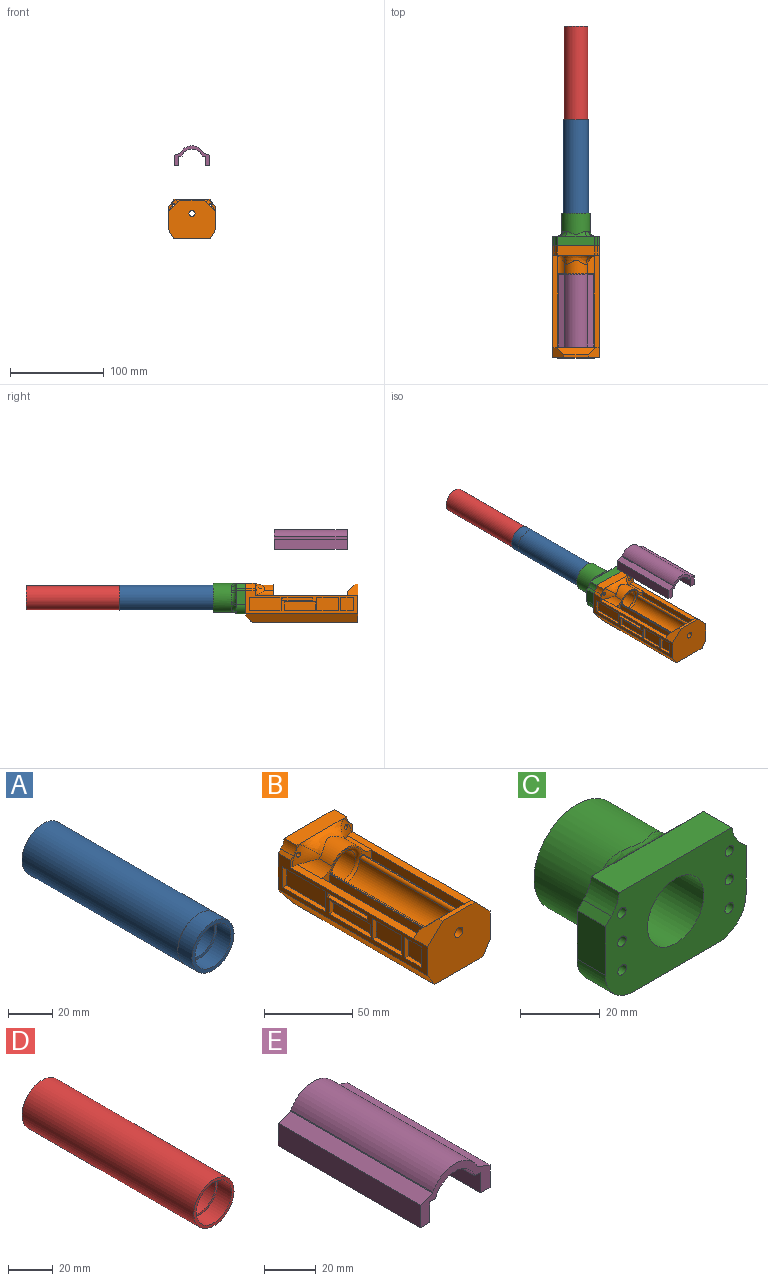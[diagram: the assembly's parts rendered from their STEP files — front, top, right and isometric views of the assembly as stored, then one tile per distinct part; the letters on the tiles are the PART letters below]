
ASSEMBLY  parts=5 mates=4
PART A: 12 faces, bbox 27.1x109x27.1 mm
  f0: plane 22.5x22.5mm, normal (0,1,0), area 83.4mm2, adj f2,f9
  f1: plane 23x23mm, normal (0,-1,0), area 101.3mm2, adj f2,f6
  f2: cylinder r=10mm len=100mm, axis (0,-1,0), area 6283.2mm2, adj f0,f1
  f3: cylinder r=13.55mm len=100mm, axis (0,-1,0), area 8513.7mm2, adj f4,f5
  f4: plane 27.1x27.1mm, normal (0,1,0), area 66.1mm2, adj f3,f10
  f5: plane 27.1x27.1mm, normal (0,-1,0), area 4.2mm2, adj f3,f7
  f6: cylinder r=11.5mm len=23mm, axis (0,1,0), area 650.3mm2, adj f1,f8
  f7: cylinder r=13.5mm len=27mm, axis (0,1,0), area 763.4mm2, adj f5,f8
  f8: plane 27x27mm, normal (0,-1,0), area 157.1mm2, adj f6,f7
  f9: cylinder r=11.25mm len=22.5mm, axis (0,1,0), area 706.9mm2, adj f0,f11
  f10: cylinder r=12.75mm len=25.5mm, axis (0,1,0), area 801.1mm2, adj f4,f11
  f11: plane 25.5x25.5mm, normal (0,1,0), area 113.1mm2, adj f9,f10
PART B: 129 faces, bbox 66.7x120x48.3 mm
  f0: plane 8.42x1.15mm, normal (0,0,-1), area 9.6mm2, adj f9,f13,f119,f127
  f1: plane 98.88x5.35mm, normal (0,0,1), area 514.2mm2, adj f5,f7,f103,f104,f105,f109,f119
  f2: plane 78.85x0.69mm, normal (0,0,1), area 54.5mm2, adj f103,f111,f119,f126
  f3: plane 78.85x0.69mm, normal (0,0,1), area 54.5mm2, adj f103,f113,f119,f125
  f4: plane 98.88x5.35mm, normal (0,0,1), area 514.2mm2, adj f6,f12,f103,f107,f108,f115,f119
  f5: plane 13x6.97mm, normal (0,-1,0), area 17.7mm2, adj f1,f7,f14,f16,f19,f105
  f6: plane 13x6.97mm, normal (0,-1,0), area 17.7mm2, adj f4,f12,f14,f17,f18,f107
  f7: plane 120x25mm, normal (-1,0,0), area 1029.4mm2, adj f1,f5,f10,f11,f16,f30,f51,f52
  f8: plane 113x38.65mm, normal (0,0,-1), area 2240.3mm2, adj f10,f30,f31,f32,f34,f36,f37,f39
  f9: cylinder r=11mm len=80.76mm, axis (0,1,0), area 2885.8mm2, adj f0,f13,f118,f119,f124,f125,f126
  f10: plane 50x40.97mm, normal (0,-1,0), area 1820.1mm2, adj f7,f8,f12,f30,f31,f120,f122,f123
  f11: plane 50x34.97mm, normal (0,1,0), area 1338.2mm2, adj f7,f12,f14,f15,f16,f17,f18,f19
  f12: plane 120x25mm, normal (1,0,0), area 1029.4mm2, adj f4,f6,f10,f11,f17,f31,f76,f77
  f13: plane 22x13.66mm, normal (0,1,0), area 217.4mm2, adj f0,f9,f118,f127
  f14: plane 40x10mm, normal (0,0,1), area 400mm2, adj f5,f6,f11,f18,f19,f106
  f15: cylinder r=10mm len=27mm, axis (0,-1,0), area 1696.5mm2, adj f11,f124
  f16: plane 10x2.15mm, normal (-0.71,0,0.71), area 30.3mm2, adj f5,f7,f11,f19
  f17: plane 10x2.15mm, normal (0.71,0,0.71), area 30.3mm2, adj f6,f11,f12,f18
  f18: cylinder r=10mm len=10mm, axis (0,1,0), area 66.3mm2, adj f6,f11,f14,f17
  f19: cylinder r=10mm len=10mm, axis (0,1,0), area 66.3mm2, adj f5,f11,f14,f16
  f20: cylinder r=1.5mm len=10.52mm, axis (0,1,0), area 97.8mm2, adj f11,f107
  f21: cylinder r=1.5mm len=25mm, axis (0,1,0), area 235.6mm2, adj f11,f22
  f22: plane 3x3mm, normal (0,1,0), area 7.1mm2, adj f21
  f23: cylinder r=1.5mm len=25mm, axis (0,1,0), area 235.6mm2, adj f11,f24
  f24: plane 3x3mm, normal (0,1,0), area 7.1mm2, adj f23
  f25: cylinder r=1.5mm len=10.52mm, axis (0,1,0), area 97.8mm2, adj f11,f105
  f26: cylinder r=1.5mm len=25mm, axis (0,1,0), area 235.6mm2, adj f11,f27
  f27: plane 3x3mm, normal (0,1,0), area 7.1mm2, adj f26
  f28: cylinder r=1.5mm len=25mm, axis (0,1,0), area 235.6mm2, adj f11,f29
  f29: plane 3x3mm, normal (0,1,0), area 7.1mm2, adj f28
  f30: plane 120x8.97mm, normal (-0.85,0,-0.53), area 1244.6mm2, adj f7,f8,f10,f11,f101
  f31: plane 120x8.97mm, normal (0.85,0,-0.53), area 1244.6mm2, adj f8,f10,f11,f12,f101
  f32: cylinder r=7.5mm len=15mm, axis (0,0,-1), area 471.2mm2, adj f8,f33
  f33: plane 15x15mm, normal (0,0,-1), area 176.7mm2, adj f32
  f34: cylinder r=7.5mm len=15mm, axis (0,0,-1), area 471.2mm2, adj f8,f35
  f35: plane 15x15mm, normal (0,0,-1), area 176.7mm2, adj f34
  f36: plane 30x5mm, normal (0,1,0), area 150mm2, adj f8,f37,f39,f40
  f37: plane 18.57x5mm, normal (1,0,0), area 88.8mm2, adj f8,f36,f38,f40,f101
  f38: plane 30x2.17mm, normal (0,-1,0), area 65.1mm2, adj f37,f39,f40,f101
  f39: plane 18.57x5mm, normal (-1,0,0), area 88.8mm2, adj f8,f36,f38,f40,f101
  f40: plane 30x18.57mm, normal (0,0,-1), area 557.1mm2, adj f36,f37,f38,f39
  f41: plane 30x5mm, normal (0,1,0), area 150mm2, adj f8,f42,f44,f45
  f42: plane 26.66x5mm, normal (1,0,0), area 133.3mm2, adj f8,f41,f43,f45
  f43: plane 30x5mm, normal (0,-1,0), area 150mm2, adj f8,f42,f44,f45
  f44: plane 26.66x5mm, normal (-1,0,0), area 133.3mm2, adj f8,f41,f43,f45
  f45: plane 30x26.66mm, normal (0,0,-1), area 799.7mm2, adj f41,f42,f43,f44
  f46: plane 16.72x5mm, normal (-1,0,0), area 83.6mm2, adj f8,f47,f49,f50
  f47: plane 30x5mm, normal (0,1,0), area 150mm2, adj f8,f46,f48,f50
  f48: plane 16.72x5mm, normal (1,0,0), area 83.6mm2, adj f8,f47,f49,f50
  f49: plane 30x5mm, normal (0,-1,0), area 150mm2, adj f8,f46,f48,f50
  f50: plane 30x16.72mm, normal (0,0,-1), area 501.7mm2, adj f46,f47,f48,f49
  f51: plane 13.47x3mm, normal (0,0,-1), area 40.4mm2, adj f7,f52,f54,f55
  f52: plane 14.37x3mm, normal (0,-1,0), area 43.1mm2, adj f7,f51,f53,f55
  f53: plane 13.47x3mm, normal (0,0,1), area 40.4mm2, adj f7,f52,f54,f55
  f54: plane 14.37x3mm, normal (0,1,0), area 43.1mm2, adj f7,f51,f53,f55
  f55: plane 14.37x13.47mm, normal (-1,0,0), area 193.6mm2, adj f51,f52,f53,f54
  f56: plane 23.27x3mm, normal (0,0,-1), area 69.8mm2, adj f7,f57,f59,f60
  f57: plane 14.21x3mm, normal (0,-1,0), area 42.6mm2, adj f7,f56,f58,f60
  f58: plane 23.27x3mm, normal (0,0,1), area 69.8mm2, adj f7,f57,f59,f60
  f59: plane 14.21x3mm, normal (0,1,0), area 42.6mm2, adj f7,f56,f58,f60
  f60: plane 23.27x14.21mm, normal (-1,0,0), area 330.8mm2, adj f56,f57,f58,f59
  f61: plane 31.97x3mm, normal (0,0,-1), area 95.9mm2, adj f7,f62,f64,f65
  f62: plane 3.08x3mm, normal (0,-1,0), area 9.2mm2, adj f7,f61,f63,f65
  f63: plane 31.97x3mm, normal (0,0,1), area 95.9mm2, adj f7,f62,f64,f65
  f64: plane 3.08x3mm, normal (0,1,0), area 9.2mm2, adj f7,f61,f63,f65
  f65: plane 31.97x3.08mm, normal (-1,0,0), area 98.5mm2, adj f61,f62,f63,f64
  f66: plane 33.34x3mm, normal (0,0,-1), area 100mm2, adj f7,f67,f69,f70
  f67: plane 9.6x3mm, normal (0,-1,0), area 28.8mm2, adj f7,f66,f68,f70
  f68: plane 33.34x3mm, normal (0,0,1), area 100mm2, adj f7,f67,f69,f70
  f69: plane 9.6x3mm, normal (0,1,0), area 28.8mm2, adj f7,f66,f68,f70
  f70: plane 33.34x9.6mm, normal (-1,0,0), area 320mm2, adj f66,f67,f68,f69
  f71: plane 33.75x3mm, normal (0,0,-1), area 101.3mm2, adj f7,f72,f74,f75
  f72: plane 14.15x3mm, normal (0,-1,0), area 42.5mm2, adj f7,f71,f73,f75
  f73: plane 33.75x3mm, normal (0,0,1), area 101.3mm2, adj f7,f72,f74,f75
  f74: plane 14.15x3mm, normal (0,1,0), area 42.5mm2, adj f7,f71,f73,f75
  f75: plane 33.75x14.15mm, normal (-1,0,0), area 477.7mm2, adj f71,f72,f73,f74
  f76: plane 13.47x3mm, normal (0,0,-1), area 40.4mm2, adj f12,f77,f79,f80
  f77: plane 14.37x3mm, normal (0,1,0), area 43.1mm2, adj f12,f76,f78,f80
  f78: plane 13.47x3mm, normal (0,0,1), area 40.4mm2, adj f12,f77,f79,f80
  f79: plane 14.37x3mm, normal (0,-1,0), area 43.1mm2, adj f12,f76,f78,f80
  f80: plane 14.37x13.47mm, normal (1,0,0), area 193.6mm2, adj f76,f77,f78,f79
  f81: plane 23.27x3mm, normal (0,0,-1), area 69.8mm2, adj f12,f82,f84,f85
  f82: plane 14.21x3mm, normal (0,1,0), area 42.6mm2, adj f12,f81,f83,f85
  f83: plane 23.27x3mm, normal (0,0,1), area 69.8mm2, adj f12,f82,f84,f85
  f84: plane 14.21x3mm, normal (0,-1,0), area 42.6mm2, adj f12,f81,f83,f85
  f85: plane 23.27x14.21mm, normal (1,0,0), area 330.8mm2, adj f81,f82,f83,f84
  f86: plane 31.97x3mm, normal (0,0,-1), area 95.9mm2, adj f12,f87,f89,f90
  f87: plane 3.08x3mm, normal (0,1,0), area 9.2mm2, adj f12,f86,f88,f90
  f88: plane 31.97x3mm, normal (0,0,1), area 95.9mm2, adj f12,f87,f89,f90
  f89: plane 3.08x3mm, normal (0,-1,0), area 9.2mm2, adj f12,f86,f88,f90
  f90: plane 31.97x3.08mm, normal (1,0,0), area 98.5mm2, adj f86,f87,f88,f89
  f91: plane 33.34x3mm, normal (0,0,-1), area 100mm2, adj f12,f92,f94,f95
  f92: plane 9.6x3mm, normal (0,1,0), area 28.8mm2, adj f12,f91,f93,f95
  f93: plane 33.34x3mm, normal (0,0,1), area 100mm2, adj f12,f92,f94,f95
  f94: plane 9.6x3mm, normal (0,-1,0), area 28.8mm2, adj f12,f91,f93,f95
  f95: plane 33.34x9.6mm, normal (1,0,0), area 320mm2, adj f91,f92,f93,f94
  f96: plane 33.75x3mm, normal (0,0,-1), area 101.3mm2, adj f12,f97,f99,f100
  f97: plane 14.15x3mm, normal (0,1,0), area 42.5mm2, adj f12,f96,f98,f100
  f98: plane 33.75x3mm, normal (0,0,1), area 101.3mm2, adj f12,f97,f99,f100
  f99: plane 14.15x3mm, normal (0,-1,0), area 42.5mm2, adj f12,f96,f98,f100
  f100: plane 33.75x14.15mm, normal (1,0,0), area 477.7mm2, adj f96,f97,f98,f99
  f101: plane 47.51x7mm, normal (0,0.71,-0.71), area 306.4mm2, adj f8,f11,f30,f31,f37,f38,f39
  f102: cylinder r=13.88mm len=23.54mm, axis (0,1,0), area 331.1mm2, adj f103,f104,f105,f106,f107,f108
  f103: plane 40.5x21.22mm, normal (0,-1,0), area 165.7mm2, adj f1,f2,f3,f4,f102,f104,f108,f109
  f104: cylinder r=10mm len=19.38mm, axis (0,1,0), area 157.5mm2, adj f1,f102,f103,f105
  f105: torus R=23.88mm, axis (0,1,0), area 125.5mm2, adj f1,f5,f25,f102,f104,f106
  f106: bspline ~37.52x10.56mm, area 254.6mm2, adj f14,f102,f105,f107
  f107: torus R=23.88mm, axis (0,1,0), area 125.5mm2, adj f4,f6,f20,f102,f106,f108
  f108: cylinder r=10mm len=19.38mm, axis (0,1,0), area 157.5mm2, adj f4,f102,f103,f107
  f109: plane 80x10mm, normal (1,0,0), area 800mm2, adj f1,f103,f110,f112,f117
  f110: plane 10x6mm, normal (0,1,0), area 60mm2, adj f109,f111,f112,f117
  f111: plane 80x10mm, normal (-1,0,0), area 800mm2, adj f2,f103,f110,f112,f117
  f112: plane 80x6mm, normal (0,0,1), area 480mm2, adj f103,f109,f110,f111
  f113: plane 80x10mm, normal (1,0,0), area 800mm2, adj f3,f103,f114,f116,f121
  f114: plane 10x6mm, normal (0,1,0), area 60mm2, adj f113,f115,f116,f121
  f115: plane 80x10mm, normal (-1,0,0), area 800mm2, adj f4,f103,f114,f116,f121
  f116: plane 80x6mm, normal (0,0,1), area 480mm2, adj f103,f113,f114,f115
  f117: plane 6x1.15mm, normal (0,0,-1), area 6.9mm2, adj f109,f110,f111,f119
  f118: plane 8.42x1.15mm, normal (0,0,-1), area 9.6mm2, adj f9,f13,f119,f127
  f119: plane 50x6.1mm, normal (0,1,0), area 183.4mm2, adj f0,f1,f2,f3,f4,f9,f117,f118
  f120: plane 26x3.15mm, normal (0,0,1), area 81.8mm2, adj f10,f122,f123,f128
  f121: plane 6x1.15mm, normal (0,0,-1), area 6.9mm2, adj f113,f114,f115,f119
  f122: plane 12x12mm, normal (0.71,0,0.71), area 143.9mm2, adj f10,f12,f119,f120,f128
  f123: plane 12x12mm, normal (-0.71,0,0.71), area 143.9mm2, adj f7,f10,f119,f120,f128
  f124: torus R=13mm, axis (0,-1,0), area 237mm2, adj f9,f15,f103,f125,f126
  f125: cylinder r=2mm len=79.62mm, axis (0,1,0), area 256.9mm2, adj f3,f9,f103,f119,f124
  f126: cylinder r=2mm len=79.62mm, axis (0,1,0), area 256.9mm2, adj f2,f9,f103,f119,f124
  f127: cylinder r=3.26mm len=11.15mm, axis (0,-1,0), area 210.7mm2, adj f0,f10,f13,f118,f119
  f128: plane 42x8mm, normal (0,0.71,0.71), area 384.7mm2, adj f119,f120,f122,f123
PART C: 38 faces, bbox 52.4x35.7x41.5 mm
  f0: plane 22.9x22.9mm, normal (0,1,0), area 97.7mm2, adj f15,f33
  f1: plane 33x14.37mm, normal (0,1,0), area 180.1mm2, adj f2,f3,f4,f5,f6,f12,f13,f14
  f2: plane 30.44x10.44mm, normal (0,0,-1), area 300mm2, adj f1,f17,f18,f21,f36,f37
  f3: plane 15x10mm, normal (-1,0,0), area 150mm2, adj f1,f4,f18,f36
  f4: plane 10x2.15mm, normal (-0.71,0,0.71), area 30.3mm2, adj f1,f3,f5,f18
  f5: cylinder r=10mm len=10mm, axis (0,-1,0), area 66.3mm2, adj f1,f4,f6,f18
  f6: plane 40.73x10.73mm, normal (0,0,1), area 400mm2, adj f1,f5,f7,f17,f18,f32
  f7: cylinder r=10mm len=10mm, axis (0,-1,0), area 66.3mm2, adj f6,f8,f17,f18
  f8: plane 10x2.15mm, normal (0.71,0,0.71), area 30.3mm2, adj f7,f16,f17,f18
  f9: cylinder r=1.5mm len=10mm, axis (0,-1,0), area 94.2mm2, adj f17,f18,f29
  f10: cylinder r=1.5mm len=10.84mm, axis (0,-1,0), area 96.9mm2, adj f17,f18,f27
  f11: cylinder r=1.5mm len=10mm, axis (0,-1,0), area 94.2mm2, adj f17,f18,f25
  f12: cylinder r=1.5mm len=10mm, axis (0,-1,0), area 94.2mm2, adj f1,f18,f24
  f13: cylinder r=1.5mm len=10.84mm, axis (0,-1,0), area 96.9mm2, adj f1,f18,f26
  f14: cylinder r=1.5mm len=10mm, axis (0,-1,0), area 94.2mm2, adj f1,f18,f28
  f15: cylinder r=10mm len=35mm, axis (0,-1,0), area 2199.1mm2, adj f0,f18
  f16: plane 15x10mm, normal (1,0,0), area 150mm2, adj f8,f17,f18,f37
  f17: plane 33x14.37mm, normal (0,1,0), area 180.1mm2, adj f2,f6,f7,f8,f9,f10,f11,f16
  f18: plane 50x33mm, normal (0,-1,0), area 1199.3mm2, adj f2,f3,f4,f5,f6,f7,f8,f9
  f19: cylinder r=15.34mm len=30.68mm, axis (0,-1,0), area 1968.2mm2, adj f20,f21,f22,f23,f24,f25,f26,f27
  f20: plane 30.68x30.68mm, normal (0,1,0), area 162.3mm2, adj f19,f34
  f21: bspline ~22.8x5.52mm, area 103.6mm2, adj f2,f19,f22,f23
  f22: torus R=20.34mm, axis (0,1,0), area 71.1mm2, adj f1,f19,f21,f24
  f23: torus R=20.34mm, axis (0,1,0), area 71.1mm2, adj f17,f19,f21,f25
  f24: bspline ~5.54x5mm, area 16.4mm2, adj f12,f19,f22,f26
  f25: bspline ~5.54x5mm, area 16.4mm2, adj f11,f19,f23,f27
  f26: torus R=20.34mm, axis (0,1,0), area 91.9mm2, adj f1,f13,f19,f24,f28
  f27: torus R=20.34mm, axis (0,1,0), area 91.9mm2, adj f10,f17,f19,f25,f29
  f28: bspline ~5.46x5mm, area 15.4mm2, adj f14,f19,f26,f30
  f29: bspline ~5.46x5mm, area 15.4mm2, adj f9,f19,f27,f31
  f30: torus R=20.34mm, axis (0,1,0), area 50.9mm2, adj f1,f19,f28,f32
  f31: torus R=20.34mm, axis (0,1,0), area 50.9mm2, adj f17,f19,f29,f32
  f32: bspline ~26.73x5.32mm, area 93.5mm2, adj f6,f19,f30,f31
  f33: cylinder r=11.45mm len=22.9mm, axis (0,1,0), area 719.4mm2, adj f0,f35
  f34: cylinder r=13.55mm len=27.1mm, axis (0,1,0), area 851.4mm2, adj f20,f35
  f35: plane 27.1x27.1mm, normal (0,1,0), area 164.9mm2, adj f33,f34
  f36: cylinder r=10mm len=10mm, axis (0,-1,0), area 157.1mm2, adj f1,f2,f3,f18
  f37: cylinder r=10mm len=10mm, axis (0,-1,0), area 157.1mm2, adj f2,f16,f17,f18
PART D: 6 faces, bbox 25.5x109x25.5 mm
  f0: plane 22.35x22.35mm, normal (0,-1,0), area 78.2mm2, adj f1,f4
  f1: cylinder r=10mm len=100mm, axis (0,-1,0), area 6283.2mm2, adj f0,f3
  f2: cylinder r=12.75mm len=109mm, axis (0,-1,0), area 8732.1mm2, adj f3,f5
  f3: plane 25.5x25.5mm, normal (0,1,0), area 196.5mm2, adj f1,f2
  f4: cylinder r=11.17mm len=22.35mm, axis (0,1,0), area 631.9mm2, adj f0,f5
  f5: plane 25.5x25.5mm, normal (0,-1,0), area 118.4mm2, adj f2,f4
PART E: 15 faces, bbox 38.4x78x20.9 mm
  f0: plane 78x9.72mm, normal (1,0,0), area 757.8mm2, adj f1,f12,f13,f14
  f1: plane 78x3.3mm, normal (0,0,-1), area 257mm2, adj f0,f2,f13,f14
  f2: cylinder r=11.34mm len=78mm, axis (0,1,0), area 2185.7mm2, adj f1,f3,f13,f14
  f3: plane 78x3.3mm, normal (0,0,-1), area 257mm2, adj f2,f4,f13,f14
  f4: plane 78x9.72mm, normal (-1,0,0), area 757.8mm2, adj f3,f5,f13,f14
  f5: plane 78x5.2mm, normal (0,0,-1), area 405.4mm2, adj f4,f6,f13,f14
  f6: plane 78x10.74mm, normal (1,0,0), area 837.9mm2, adj f5,f7,f13,f14
  f7: plane 78x6.76mm, normal (0.34,0,0.94), area 559.9mm2, adj f6,f8,f13,f14
  f8: cylinder r=13.77mm len=78mm, axis (0,1,0), area 2375.7mm2, adj f7,f9,f13,f14
  f9: cylinder r=10mm len=78mm, axis (0,1,0), area 34.4mm2, adj f8,f10,f13,f14
  f10: plane 78x6.76mm, normal (-0.34,0,0.94), area 559.9mm2, adj f9,f11,f13,f14
  f11: plane 78x10.74mm, normal (-1,0,0), area 837.9mm2, adj f10,f12,f13,f14
  f12: plane 78x5.2mm, normal (0,0,-1), area 405.4mm2, adj f0,f11,f13,f14
  f13: plane 38.4x20.93mm, normal (0,-1,0), area 236.1mm2, adj f0,f1,f2,f3,f4,f5,f6,f7
  f14: plane 38.4x20.93mm, normal (0,1,0), area 236.1mm2, adj f0,f1,f2,f3,f4,f5,f6,f7
PLACE A t=(-9.34,-143.84,115.62)mm
PLACE B t=(-9.34,-123.84,115.62)mm
PLACE C t=(-9.34,-133.84,115.62)mm
PLACE D t=(-9.34,-153.84,115.62)mm
PLACE E t=(-9.34,-123.77,174.28)mm
MATE fastened C.f15 <-> B.f9  axis (0,-1,0) through (-9.34,-53.95,106.64)mm
MATE fastened D.f1 <-> A.f2  axis (0,-1,0) through (-9.34,81.05,106.64)mm
MATE slider E.f1 <-> B.f2  axis (0,0,-1) through (-21.67,-123.38,168.19)mm
MATE fastened A.f2 <-> C.f15  axis (0,-1,0) through (-9.34,-18.95,106.64)mm
